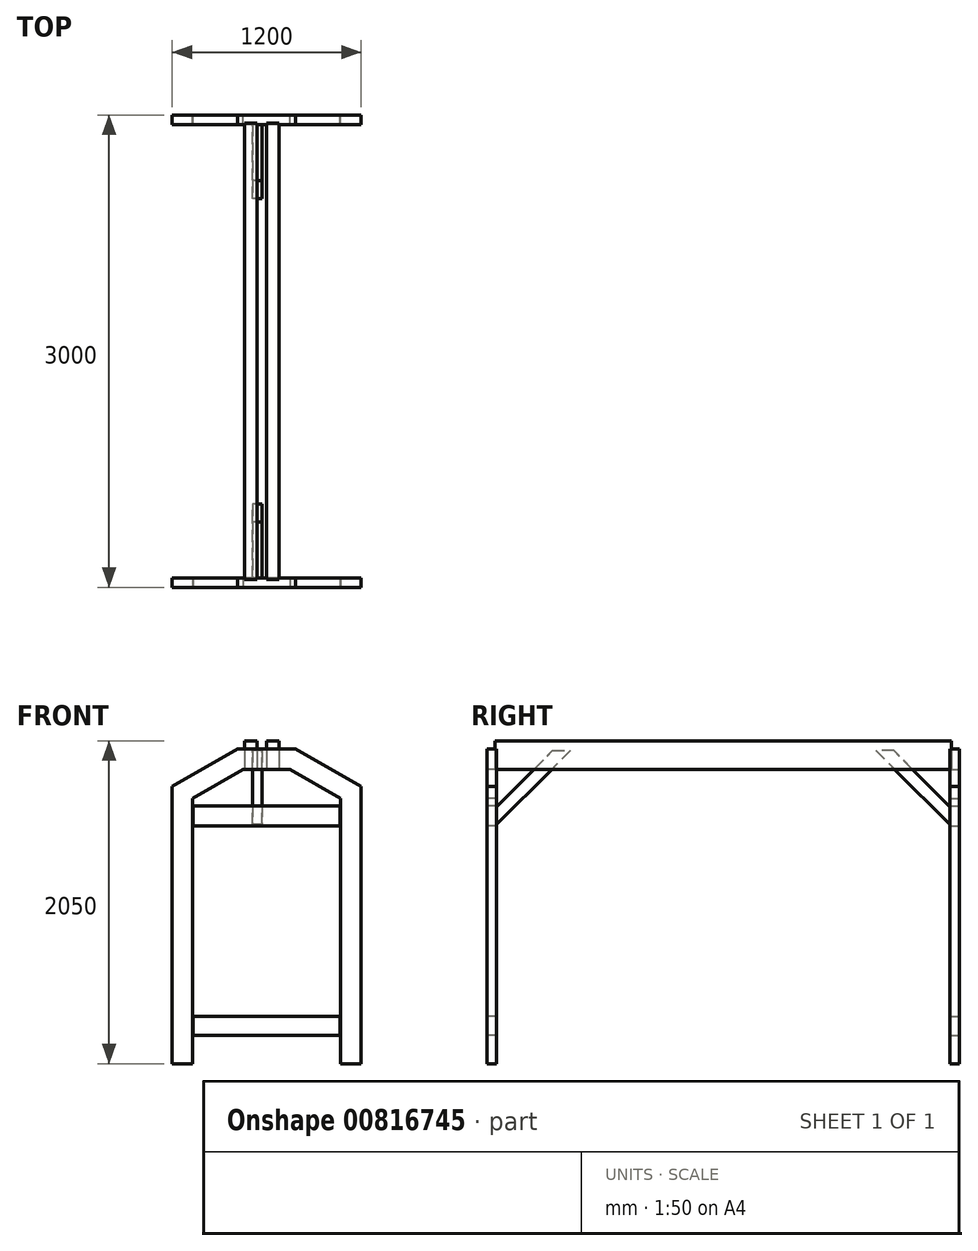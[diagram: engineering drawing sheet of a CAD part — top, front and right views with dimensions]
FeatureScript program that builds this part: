
annotation { "Feature Type Name" : "Feature", "Feature Type Description" : "" }
export const myFeature = defineFeature(function(context is Context, id is Id, definition is map)
    precondition{}
    {
        {
            var Q0;
            Q0=qCreatedBy(makeId("Front.planeOp"),FACE);
            var sketch = newSketch(context, id + "F0", { "sketchPlane" : qUnion([Q0])});
            skLineSegment(sketch, "E0", {"start": v(-184.83, 2000) * mm, "end": v(0, 2000) * mm});
            skLineSegment(sketch, "E1", {"start": v(-184.83, 2000) * mm, "end": v(-600, 1760.3) * mm});
            skLineSegment(sketch, "E2", {"start": v(-600, 1760.3) * mm, "end": v(-600, 0) * mm});
            skLineSegment(sketch, "E3", {"start": v(0, 2000) * mm, "end": v(0, 0) * mm, "construction": true});
            skLineSegment(sketch, "E4.MirrorCS", {"start": v(600, 1760.3) * mm, "end": v(600, 0) * mm});
            skLineSegment(sketch, "E5.MirrorCS", {"start": v(184.83, 2000) * mm, "end": v(0, 2000) * mm});
            skLineSegment(sketch, "E6.MirrorCS", {"start": v(184.83, 2000) * mm, "end": v(600, 1760.3) * mm});
            skLineSegment(sketch, "E7", {"start": v(0, 1870) * mm, "end": v(-150, 1870) * mm});
            skLineSegment(sketch, "E8", {"start": v(-150, 1870) * mm, "end": v(-470, 1685.25) * mm});
            skLineSegment(sketch, "E9", {"start": v(-470, 1685.25) * mm, "end": v(-470, 0) * mm});
            skLineSegment(sketch, "E10", {"start": v(-470, 0) * mm, "end": v(-600, 0) * mm});
            skLineSegment(sketch, "E11", {"start": v(-535, 1797.83) * mm, "end": v(-470, 1685.25) * mm, "construction": true});
            skLineSegment(sketch, "E12", {"start": v(-150, 2000) * mm, "end": v(-150, 1870) * mm, "construction": true});
            skLineSegment(sketch, "E13.MirrorCS", {"start": v(470, 0) * mm, "end": v(600, 0) * mm});
            skLineSegment(sketch, "E14.MirrorCS", {"start": v(470, 1685.25) * mm, "end": v(470, 0) * mm});
            skLineSegment(sketch, "E15.MirrorCS", {"start": v(0, 1870) * mm, "end": v(150, 1870) * mm});
            skLineSegment(sketch, "E16.MirrorCS", {"start": v(150, 1870) * mm, "end": v(470, 1685.25) * mm});
            skSolve(sketch);
        }
        {
            var Q0;
            Q0=makeQuery(id+"F0.imprint","IMPRINT",FACE,{"disambiguationData":[TD([[makeQuery(id+"F0.imprint","IMPRINT",EDGE,{"derivedFrom":sQuery(id+"F0.wireOp",EDGE,"E0")}),-1.0]])]});
            extrude(context, id + "F1", {"entities" : qUnion([Q0]), "depth" : 60 * mm, "offsetDistance" : 25 * mm});
        }
        {
            var Q0;
            Q0=qCreatedBy(makeId("Front.planeOp"),FACE);
            cPlane(context, id + "F2", {"entities" : qUnion([Q0]), "cplaneType" : CPlaneType.OFFSET, "offset" : 3000 * mm, "width" : 150 * mm, "height" : 150 * mm});
        }
        {
            var Q0;
            Q0=qCreatedBy(id+"F2.planeOp",FACE);
            var sketch = newSketch(context, id + "F3", { "sketchPlane" : qUnion([Q0])});
            skLineSegment(sketch, "E17.0.0", {"start": v(-150, 1870) * mm, "end": v(150, 1870) * mm});
            skLineSegment(sketch, "E17.0.1", {"start": v(150, 1870) * mm, "end": v(470, 1685.25) * mm});
            skLineSegment(sketch, "E17.0.2", {"start": v(470, 1685.25) * mm, "end": v(470, 0) * mm});
            skLineSegment(sketch, "E17.0.3", {"start": v(470, 0) * mm, "end": v(600, 0) * mm});
            skLineSegment(sketch, "E17.0.4", {"start": v(600, 0) * mm, "end": v(600, 1760.3) * mm});
            skLineSegment(sketch, "E17.0.5", {"start": v(600, 1760.3) * mm, "end": v(184.83, 2000) * mm});
            skLineSegment(sketch, "E17.0.6", {"start": v(184.83, 2000) * mm, "end": v(-184.83, 2000) * mm});
            skLineSegment(sketch, "E17.0.7", {"start": v(-184.83, 2000) * mm, "end": v(-600, 1760.3) * mm});
            skLineSegment(sketch, "E17.0.8", {"start": v(-600, 1760.3) * mm, "end": v(-600, 0) * mm});
            skLineSegment(sketch, "E17.0.9", {"start": v(-600, 0) * mm, "end": v(-470, 0) * mm});
            skLineSegment(sketch, "E17.0.10", {"start": v(-470, 0) * mm, "end": v(-470, 1685.25) * mm});
            skLineSegment(sketch, "E17.0.11", {"start": v(-470, 1685.25) * mm, "end": v(-150, 1870) * mm});
            skSolve(sketch);
        }
        {
            var Q0;
            Q0=makeQuery(id+"F3.imprint","IMPRINT",FACE,{"disambiguationData":[TD([[makeQuery(id+"F3.imprint","IMPRINT",EDGE,{"derivedFrom":sQuery(id+"F3.wireOp",EDGE,"E17.0.0")}),1.0]])]});
            extrude(context, id + "F4", {"entities" : qUnion([Q0]), "oppositeDirection" : true, "depth" : 60 * mm, "offsetDistance" : 25 * mm});
        }
        {
            var Q0;
            Q0=qCreatedBy(makeId("Front.planeOp"),FACE);
            var sketch = newSketch(context, id + "F5", { "sketchPlane" : qUnion([Q0])});
            skLineSegment(sketch, "E18.bottom", {"start": v(-140, 2050) * mm, "end": v(-60, 2050) * mm});
            skLineSegment(sketch, "E18.top", {"start": v(-140, 1870) * mm, "end": v(-60, 1870) * mm});
            skLineSegment(sketch, "E18.left", {"start": v(-140, 2050) * mm, "end": v(-140, 1870) * mm});
            skLineSegment(sketch, "E18.right", {"start": v(-60, 2050) * mm, "end": v(-60, 1870) * mm});
            skLineSegment(sketch, "E19.bottom", {"start": v(0, 2050) * mm, "end": v(80, 2050) * mm});
            skLineSegment(sketch, "E19.top", {"start": v(0, 1870) * mm, "end": v(80, 1870) * mm});
            skLineSegment(sketch, "E19.left", {"start": v(0, 2050) * mm, "end": v(0, 1870) * mm});
            skLineSegment(sketch, "E19.right", {"start": v(80, 2050) * mm, "end": v(80, 1870) * mm});
            skSolve(sketch);
        }
        {
            var Q0;
            Q0 = qSketchRegion(id + "F5", true);
            extrude(context, id + "F6", {"entities" : qUnion([Q0]), "depth" : 2950 * mm, "offsetDistance" : 25 * mm, "hasSecondDirection" : true, "secondDirectionOppositeDirection" : false, "secondDirectionDepth" : 50 * mm});
        }
        {
            var Q0;
            Q0=qCreatedBy(id+"F2.planeOp",FACE);
            var sketch = newSketch(context, id + "F7", { "sketchPlane" : qUnion([Q0])});
            skLineSegment(sketch, "E20.bottom", {"start": v(-467.28, 1638.5) * mm, "end": v(467.28, 1638.5) * mm});
            skLineSegment(sketch, "E20.top", {"start": v(-467.28, 1510.7) * mm, "end": v(467.28, 1510.7) * mm});
            skLineSegment(sketch, "E20.left", {"start": v(-467.28, 1638.5) * mm, "end": v(-467.28, 1510.7) * mm});
            skLineSegment(sketch, "E20.right", {"start": v(467.28, 1638.5) * mm, "end": v(467.28, 1510.7) * mm});
            skLineSegment(sketch, "E21.bottom", {"start": v(-467.28, 299.22) * mm, "end": v(467.28, 299.22) * mm});
            skLineSegment(sketch, "E21.top", {"start": v(-467.28, 179.4) * mm, "end": v(467.28, 179.4) * mm});
            skLineSegment(sketch, "E21.left", {"start": v(-467.28, 299.22) * mm, "end": v(-467.28, 179.4) * mm});
            skLineSegment(sketch, "E21.right", {"start": v(467.28, 299.22) * mm, "end": v(467.28, 179.4) * mm});
            skSolve(sketch);
        }
        {
            var Q0;
            Q0 = qSketchRegion(id + "F7", true);
            extrude(context, id + "F8", {"entities" : qUnion([Q0]), "oppositeDirection" : true, "depth" : 60 * mm, "offsetDistance" : 25 * mm});
        }
        {
            var Q0;
            Q0=qCreatedBy(makeId("Front.planeOp"),FACE);
            var sketch = newSketch(context, id + "F9", { "sketchPlane" : qUnion([Q0])});
            skLineSegment(sketch, "E22.0.0", {"start": v(-467.28, 1638.5) * mm, "end": v(-467.28, 1510.7) * mm});
            skLineSegment(sketch, "E22.0.1", {"start": v(-467.28, 1510.7) * mm, "end": v(467.28, 1510.7) * mm});
            skLineSegment(sketch, "E22.0.2", {"start": v(467.28, 1510.7) * mm, "end": v(467.28, 1638.5) * mm});
            skLineSegment(sketch, "E22.0.3", {"start": v(467.28, 1638.5) * mm, "end": v(-467.28, 1638.5) * mm});
            skLineSegment(sketch, "E23.0.0", {"start": v(-467.28, 299.22) * mm, "end": v(-467.28, 179.4) * mm});
            skLineSegment(sketch, "E23.0.1", {"start": v(-467.28, 179.4) * mm, "end": v(467.28, 179.4) * mm});
            skLineSegment(sketch, "E23.0.2", {"start": v(467.28, 179.4) * mm, "end": v(467.28, 299.22) * mm});
            skLineSegment(sketch, "E23.0.3", {"start": v(467.28, 299.22) * mm, "end": v(-467.28, 299.22) * mm});
            skSolve(sketch);
        }
        {
            var Q0;
            Q0 = qSketchRegion(id + "F9", true);
            extrude(context, id + "F10", {"entities" : qUnion([Q0]), "depth" : 60 * mm, "offsetDistance" : 25 * mm});
        }
        {
            var Q0;
            Q0=makeQuery(id+"F6.opExtrude","SWEPT_FACE",FACE,{"disambiguationData":[OSD([sQuery(id+"F5.wireOp",EDGE,"E18.right")])]});
            var sketch = newSketch(context, id + "F11", { "sketchPlane" : qUnion([Q0])});
            skLineSegment(sketch, "E24", {"start": v(-2940, 1631.74) * mm, "end": v(-2583.75, 1988) * mm});
            skLineSegment(sketch, "E25", {"start": v(-2583.75, 1988) * mm, "end": v(-2470.62, 1988) * mm});
            skLineSegment(sketch, "E26", {"start": v(-2470.62, 1988) * mm, "end": v(-2940, 1518.6) * mm});
            skLineSegment(sketch, "E27", {"start": v(-2940, 1518.6) * mm, "end": v(-2940, 1631.74) * mm});
            skLineSegment(sketch, "E28", {"start": v(-1500, 1870) * mm, "end": v(-1500, 1158.19) * mm, "construction": true});
            skLineSegment(sketch, "E29.MirrorCS", {"start": v(-529.38, 1988) * mm, "end": v(-60, 1518.6) * mm});
            skLineSegment(sketch, "E30.MirrorCS", {"start": v(-416.25, 1988) * mm, "end": v(-529.38, 1988) * mm});
            skLineSegment(sketch, "E31.MirrorCS", {"start": v(-60, 1631.74) * mm, "end": v(-416.25, 1988) * mm});
            skLineSegment(sketch, "E32.MirrorCS", {"start": v(-60, 1518.6) * mm, "end": v(-60, 1631.74) * mm});
            skSolve(sketch);
        }
        {
            var Q0;
            Q0 = qSketchRegion(id + "F11", true);
            extrude(context, id + "F12", {"entities" : qUnion([Q0]), "endBound" : BoundingType.SYMMETRIC, "depth" : 60 * mm, "offsetDistance" : 25 * mm});
        }
    });
